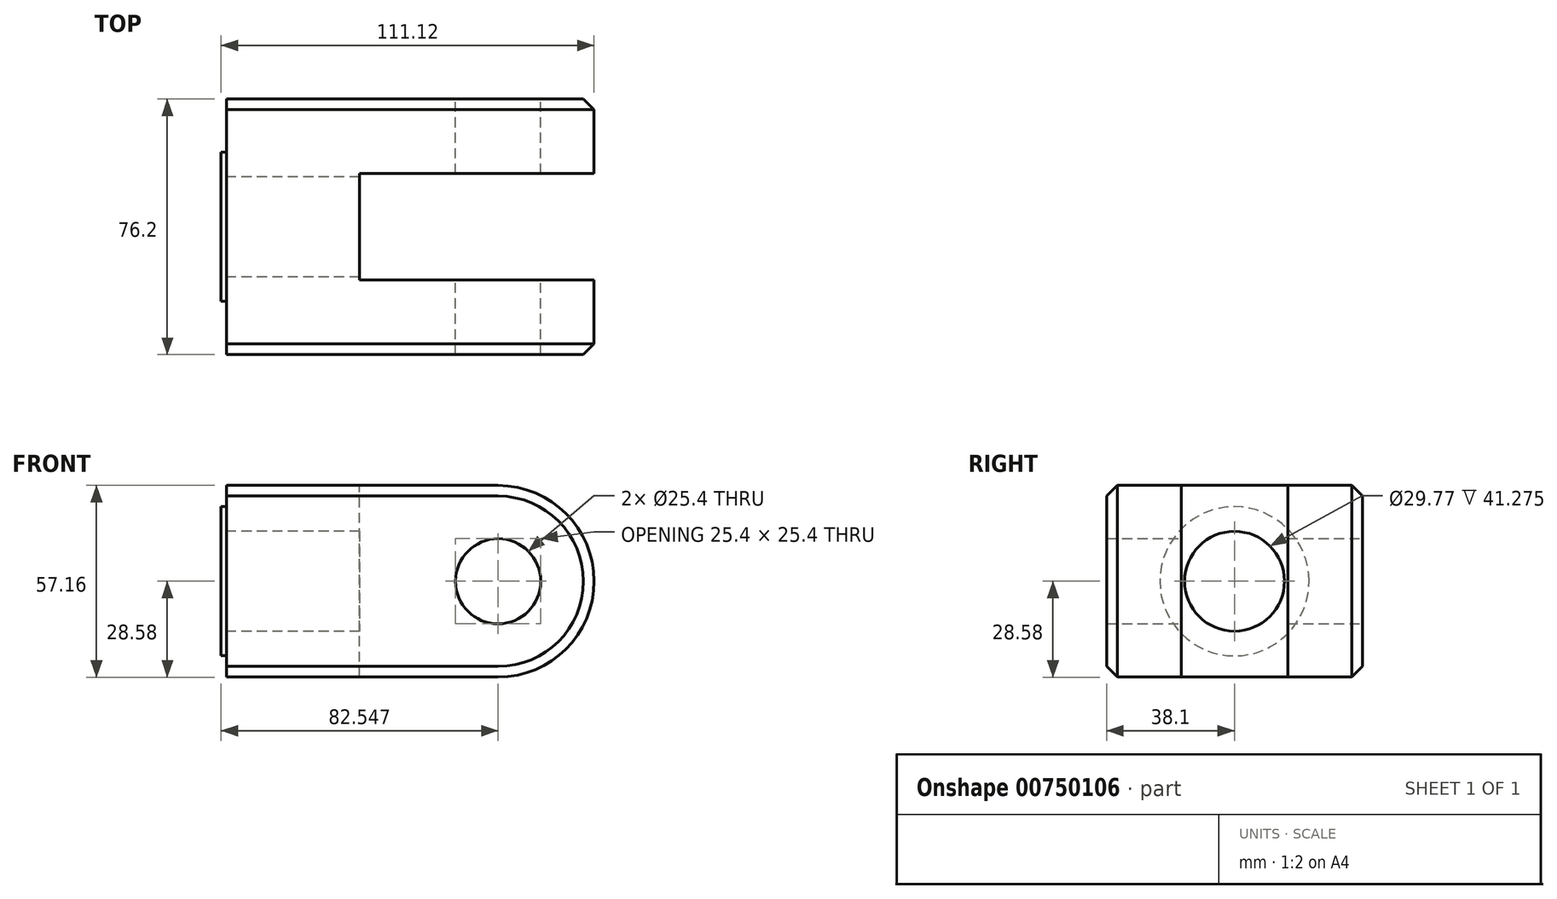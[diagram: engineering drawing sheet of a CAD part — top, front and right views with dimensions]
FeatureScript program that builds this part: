
annotation { "Feature Type Name" : "Feature", "Feature Type Description" : "" }
export const myFeature = defineFeature(function(context is Context, id is Id, definition is map)
    precondition{}
    {
        {
            var Q0;
            Q0=qCreatedBy(makeId("Front.planeOp"),FACE);
            var sketch = newSketch(context, id + "F0", { "sketchPlane" : qUnion([Q0])});
            skLineSegment(sketch, "E0.bottom", {"start": v(-55.56, -28.58) * mm, "end": v(55.56, -28.58) * mm, "construction": true});
            skLineSegment(sketch, "E0.top", {"start": v(-55.56, 28.58) * mm, "end": v(55.56, 28.58) * mm, "construction": true});
            skLineSegment(sketch, "E0.left", {"start": v(-55.56, -28.58) * mm, "end": v(-55.56, 28.58) * mm});
            skLineSegment(sketch, "E0.right", {"start": v(55.56, -28.58) * mm, "end": v(55.56, 28.58) * mm, "construction": true});
            skPoint(sketch, "E0.middle", {"position": v(0, 0) * mm});
            skCircle(sketch, "E1", {"center": v(26.99, 0) * mm, "radius": 12.7 * mm});
            skArc(sketch, "E2", {"start": v(26.99, 28.58) * mm, "mid": v(55.56, 0) * mm, "end": v(26.99, -28.58) * mm});
            skLineSegment(sketch, "E3", {"start": v(26.99, 28.58) * mm, "end": v(-55.56, 28.58) * mm});
            skLineSegment(sketch, "E4", {"start": v(26.99, -28.58) * mm, "end": v(-55.56, -28.58) * mm});
            skSolve(sketch);
        }
        {
            var Q0;
            Q0 = qSketchRegion(id + "F0", true);
            extrude(context, id + "F1", {"entities" : qUnion([Q0]), "endBound" : BoundingType.SYMMETRIC, "depth" : 76.2 * mm, "offsetDistance" : 25.4 * mm});
        }
        {
            var Q0;
            Q0=qCreatedBy(makeId("Top.planeOp"),FACE);
            var sketch = newSketch(context, id + "F2", { "sketchPlane" : qUnion([Q0])});
            skLineSegment(sketch, "E5.0", {"start": v(39.69, -38.1) * mm, "end": v(14.29, -38.1) * mm});
            skLineSegment(sketch, "E6", {"start": v(55.56, 19.05) * mm, "end": v(55.56, 0) * mm});
            skLineSegment(sketch, "E7.0", {"start": v(26.99, 38.1) * mm, "end": v(55.56, 38.1) * mm});
            skLineSegment(sketch, "E8.0", {"start": v(26.99, 38.1) * mm, "end": v(-55.56, 38.1) * mm});
            skLineSegment(sketch, "E9", {"start": v(55.56, 19.05) * mm, "end": v(55.56, -19.05) * mm});
            skLineSegment(sketch, "E10.0", {"start": v(26.99, -38.1) * mm, "end": v(-55.56, -38.1) * mm});
            skLineSegment(sketch, "E11", {"start": v(55.56, 15.88) * mm, "end": v(-14.29, 15.87) * mm});
            skLineSegment(sketch, "E12", {"start": v(-14.29, 15.88) * mm, "end": v(-14.29, 0) * mm});
            skLineSegment(sketch, "E13.MirrorCS", {"start": v(55.56, -15.88) * mm, "end": v(-14.29, -15.87) * mm});
            skLineSegment(sketch, "E14.MirrorCS", {"start": v(-14.29, -15.88) * mm, "end": v(-14.29, 0) * mm});
            skSolve(sketch);
        }
        {
            var Q0;
            Q0 = qSketchRegion(id + "F2", true);
            extrude(context, id + "F3", {"entities" : qUnion([Q0]), "operationType" : NewBodyOperationType.REMOVE, "endBound" : BoundingType.SYMMETRIC, "oppositeDirection" : true, "depth" : 76.2 * mm, "offsetDistance" : 25.4 * mm});
        }
        {
            var Q0;
            Q0=makeQuery(id+"F1.opExtrude","SWEPT_FACE",FACE,{"disambiguationData":[OSD([sQuery(id+"F0.wireOp",EDGE,"E0.left")])]});
            var sketch = newSketch(context, id + "F4", { "sketchPlane" : qUnion([Q0])});
            skPoint(sketch, "E15", {"position": v(0, 0) * mm});
            skCircle(sketch, "E16", {"center": v(0, 0) * mm, "radius": 22.23 * mm});
            skSolve(sketch);
        }
        {
            var Q0;
            Q0=sQuery(id+"F4.wireOp",VERTEX,"E15");
            var Q1;
            Q1=makeQuery(id+"F1.opExtrude","SWEPT_BODY",BODY,{"disambiguationData":[OSD([sQuery(id+"F0.wireOp",EDGE,"E0.left"),sQuery(id+"F0.wireOp",EDGE,"E1"),sQuery(id+"F0.wireOp",EDGE,"E2"),sQuery(id+"F0.wireOp",EDGE,"E3"),sQuery(id+"F0.wireOp",EDGE,"E4")])]});
            hole(context, id + "F5", {"style" : HoleStyle.SIMPLE, "endStyle" : HoleEndStyle.THROUGH, "standardTappedOrClearance" : lookupTablePath({ "standard" : "ANSI", "engagement" : "75%", "pitch" : "12 tpi", "size" : "1 1/4", "type" : "Tapped" }), "standardBlindInLast" : lookupTablePath({ "standard" : "ANSI", "engagement" : "75%", "pitch" : "12 tpi", "size" : "1 1/4", "type" : "Tapped" }), "holeDiameter" : 29.77 * mm, "majorDiameter" : 31.75 * mm, "showTappedDepth" : true, "isTappedThrough" : true, "tappedDepth" : 12.7 * mm, "tapClearance" : 3, "locations" : qUnion([Q0]), "scope" : qUnion([Q1])});
        }
        {
            var Q0;
            Q0=makeQuery(id+"F4.imprint","IMPRINT",FACE,{"disambiguationData":[TD([[makeQuery(id+"F4.imprint","IMPRINT",EDGE,{"derivedFrom":sQuery(id+"F4.wireOp",EDGE,"E16")}),-1.0]])]});
            extrude(context, id + "F6", {"entities" : qUnion([Q0]), "operationType" : NewBodyOperationType.REMOVE, "oppositeDirection" : true, "depth" : 1.59 * mm, "offsetDistance" : 25.4 * mm});
        }
        {
            var Q0;
            Q0=makeQuery(id+"F1.opExtrude","CAP_EDGE",EDGE,{"disambiguationData":[OSD([sQuery(id+"F0.wireOp",EDGE,"E3")])],"isStart":true});
            var Q1;
            Q1=makeQuery(id+"F1.opExtrude","CAP_EDGE",EDGE,{"disambiguationData":[OSD([sQuery(id+"F0.wireOp",EDGE,"E4")])],"isStart":false});
            chamfer(context, id + "F7", {"entities" : qUnion([Q0, Q1]), "width" : 3.17 * mm, "tangentPropagation" : true});
        }
    });
